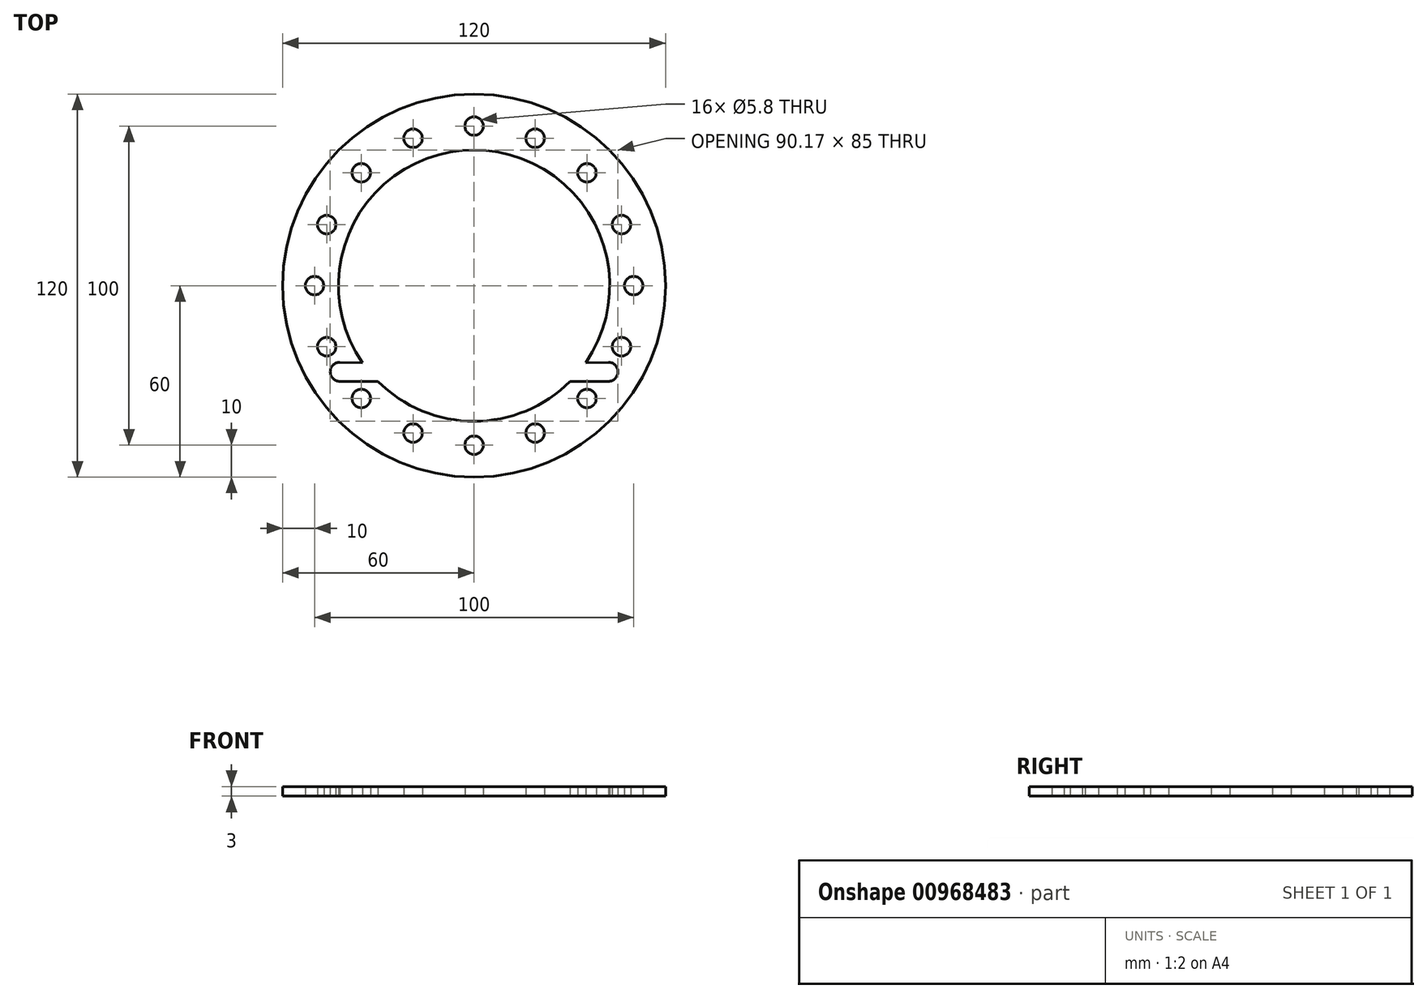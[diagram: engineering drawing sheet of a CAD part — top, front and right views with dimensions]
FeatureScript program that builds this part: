
annotation { "Feature Type Name" : "Feature", "Feature Type Description" : "" }
export const myFeature = defineFeature(function(context is Context, id is Id, definition is map)
    precondition{}
    {
        {
            var Q0;
            Q0=qCreatedBy(makeId("Top.planeOp"),FACE);
            var sketch = newSketch(context, id + "F0", { "sketchPlane" : qUnion([Q0])});
            skCircle(sketch, "E0", {"center": v(0, 0) * mm, "radius": 60 * mm});
            skArc(sketch, "E1", {"start": v(34.98, -24.13) * mm, "mid": v(0, 42.5) * mm, "end": v(-34.98, -24.13) * mm});
            skCircle(sketch, "E2", {"center": v(0, 0) * mm, "radius": 50 * mm, "construction": true});
            skCircle(sketch, "E3", {"center": v(0, 50) * mm, "radius": 2.9 * mm});
            skCircle(sketch, "E4.1.0", {"center": v(-19.13, 46.2) * mm, "radius": 2.9 * mm});
            skCircle(sketch, "E4.2.0", {"center": v(-35.36, 35.36) * mm, "radius": 2.9 * mm});
            skCircle(sketch, "E4.3.0", {"center": v(-46.2, 19.13) * mm, "radius": 2.9 * mm});
            skCircle(sketch, "E4.4.0", {"center": v(-50, 0) * mm, "radius": 2.9 * mm});
            skCircle(sketch, "E4.5.0", {"center": v(-46.2, -19.13) * mm, "radius": 2.9 * mm});
            skCircle(sketch, "E4.6.0", {"center": v(-35.36, -35.36) * mm, "radius": 2.9 * mm});
            skCircle(sketch, "E4.7.0", {"center": v(-19.13, -46.2) * mm, "radius": 2.9 * mm});
            skCircle(sketch, "E4.8.0", {"center": v(0, -50) * mm, "radius": 2.9 * mm});
            skCircle(sketch, "E4.9.0", {"center": v(19.13, -46.2) * mm, "radius": 2.9 * mm});
            skCircle(sketch, "E4.10.0", {"center": v(35.36, -35.36) * mm, "radius": 2.9 * mm});
            skCircle(sketch, "E4.11.0", {"center": v(46.2, -19.13) * mm, "radius": 2.9 * mm});
            skCircle(sketch, "E4.12.0", {"center": v(50, 0) * mm, "radius": 2.9 * mm});
            skCircle(sketch, "E4.13.0", {"center": v(46.2, 19.13) * mm, "radius": 2.9 * mm});
            skCircle(sketch, "E4.14.0", {"center": v(35.36, 35.36) * mm, "radius": 2.9 * mm});
            skCircle(sketch, "E4.15.0", {"center": v(19.13, 46.2) * mm, "radius": 2.9 * mm});
            skArc(sketch, "E5.11.0", {"start": v(42.08, -30) * mm, "mid": v(45.08, -27) * mm, "end": v(42.08, -24) * mm});
            skArc(sketch, "E6.5.0", {"start": v(-42.08, -24) * mm, "mid": v(-45.08, -27) * mm, "end": v(-42.08, -30) * mm});
            skLineSegment(sketch, "E7", {"start": v(-42.08, -30) * mm, "end": v(-30.1, -30) * mm});
            skLineSegment(sketch, "E8.trimOffspring", {"start": v(30.1, -30) * mm, "end": v(42.08, -30) * mm});
            skLineSegment(sketch, "E9.trimOffspring", {"start": v(34.98, -24.13) * mm, "end": v(42.08, -24) * mm});
            skLineSegment(sketch, "E10.trimOffspring", {"start": v(-42.08, -24) * mm, "end": v(-34.98, -24.13) * mm});
            skArc(sketch, "E11.trimOffspring", {"start": v(-30.1, -30) * mm, "mid": v(0, -42.5) * mm, "end": v(30.1, -30) * mm});
            skSolve(sketch);
        }
        {
            var Q0;
            Q0=makeQuery(id+"F0.imprint","IMPRINT",FACE,{"disambiguationData":[TD([[makeQuery(id+"F0.imprint","IMPRINT",EDGE,{"derivedFrom":sQuery(id+"F0.wireOp",EDGE,"E0")}),1.0]])]});
            extrude(context, id + "F1", {"entities" : qUnion([Q0]), "depth" : 3 * mm, "offsetDistance" : 25 * mm});
        }
    });
